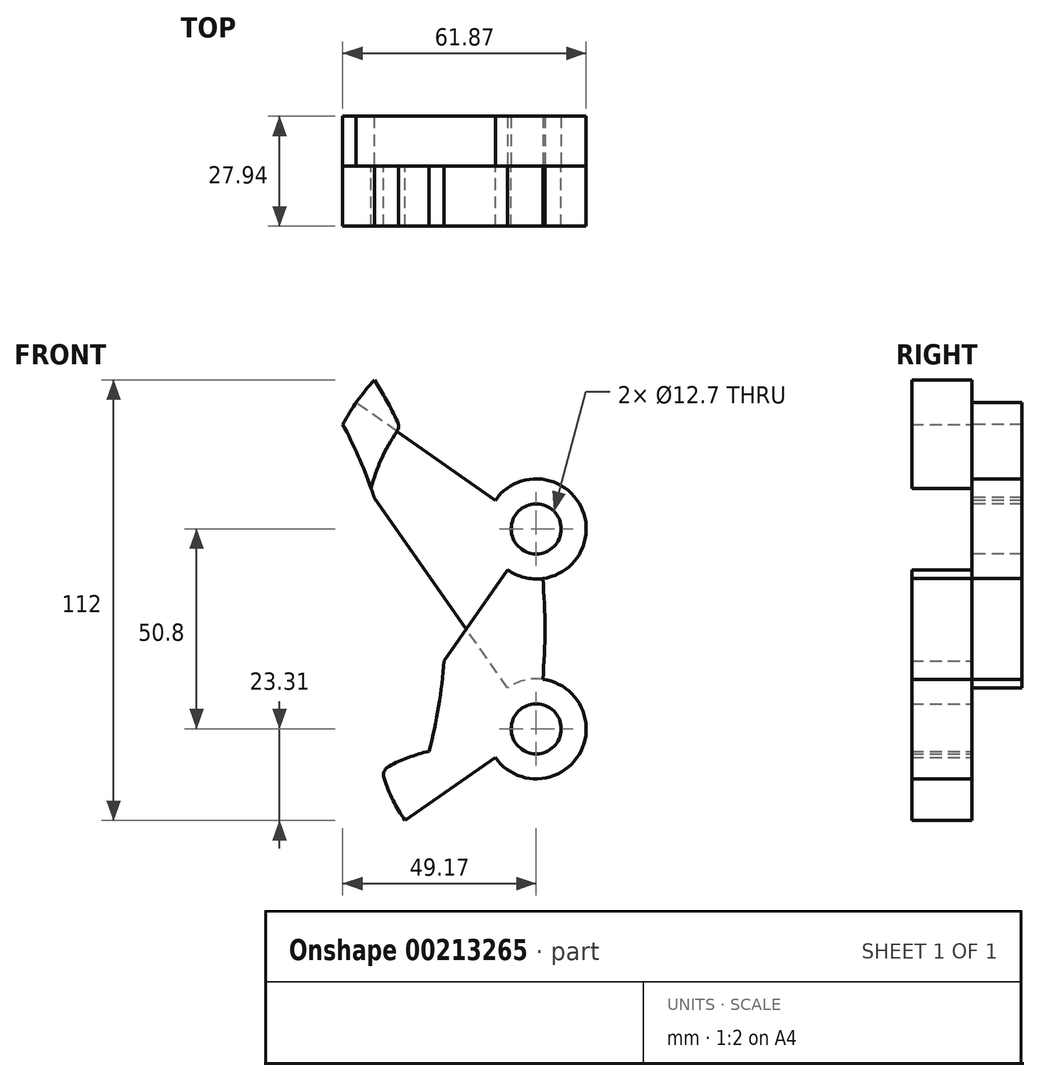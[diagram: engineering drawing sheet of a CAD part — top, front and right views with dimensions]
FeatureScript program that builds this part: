
annotation { "Feature Type Name" : "Feature", "Feature Type Description" : "" }
export const myFeature = defineFeature(function(context is Context, id is Id, definition is map)
    precondition{}
    {
        {
            var Q0;
            Q0=qCreatedBy(makeId("Front.planeOp"),FACE);
            var sketch = newSketch(context, id + "F0", { "sketchPlane" : qUnion([Q0])});
            skCircle(sketch, "E0", {"center": v(0, 0) * mm, "radius": 6.35 * mm});
            skCircle(sketch, "E1", {"center": v(0, 0) * mm, "radius": 12.7 * mm});
            skCircle(sketch, "E2", {"center": v(0, 50.8) * mm, "radius": 6.35 * mm});
            skCircle(sketch, "E3", {"center": v(0, 50.8) * mm, "radius": 12.7 * mm});
            skLineSegment(sketch, "E4", {"start": v(0, 0) * mm, "end": v(0, 50.8) * mm, "construction": true});
            skArc(sketch, "E5", {"start": v(-17.37, -47.74) * mm, "mid": v(0, 0) * mm, "end": v(0, 50.8) * mm});
            skLineSegment(sketch, "E6", {"start": v(-144.05, 25.4) * mm, "end": v(0, 0) * mm, "construction": true});
            skLineSegment(sketch, "E7", {"start": v(-144.05, 25.4) * mm, "end": v(0, 50.8) * mm, "construction": true});
            skLineSegment(sketch, "E8", {"start": v(0, 50.8) * mm, "end": v(-98.52, 119.79) * mm});
            skLineSegment(sketch, "E9", {"start": v(0, 50.8) * mm, "end": v(-66.69, -44.44) * mm});
            skLineSegment(sketch, "E10", {"start": v(0, 0) * mm, "end": v(-71.6, 102.25) * mm});
            skLineSegment(sketch, "E11", {"start": v(0, 0) * mm, "end": v(-89.4, -62.6) * mm});
            skArc(sketch, "E12", {"start": v(-41.27, -38.22) * mm, "mid": v(-23.24, 29.23) * mm, "end": v(-45.5, 95.4) * mm});
            skArc(sketch, "E13", {"start": v(-59.79, -42.43) * mm, "mid": v(-36.4, 36.04) * mm, "end": v(-74.7, 108.42) * mm});
            skLineSegment(sketch, "E14", {"start": v(-144.05, 25.4) * mm, "end": v(36.46, -78.82) * mm, "construction": true});
            skArc(sketch, "E15", {"start": v(-42.88, -12.9) * mm, "mid": v(-35.43, -8.51) * mm, "end": v(-27.25, -5.7) * mm});
            skArc(sketch, "E16", {"start": v(-37.97, 4.2) * mm, "mid": v(-31.34, 6.37) * mm, "end": v(-24.48, 7.69) * mm});
            skArc(sketch, "E17", {"start": v(-35.89, 24.01) * mm, "mid": v(-30.38, 30.68) * mm, "end": v(-23.65, 36.12) * mm});
            skArc(sketch, "E18", {"start": v(-37.12, 41.77) * mm, "mid": v(-31.63, 46.07) * mm, "end": v(-25.64, 49.65) * mm});
            skArc(sketch, "E19", {"start": v(-41.94, 61.1) * mm, "mid": v(-39.04, 69.24) * mm, "end": v(-34.58, 76.66) * mm});
            skArc(sketch, "E20", {"start": v(-49.17, 77.35) * mm, "mid": v(-45.48, 83.27) * mm, "end": v(-41.07, 88.7) * mm});
            skArc(sketch, "E21", {"start": v(-40.3, -5.22) * mm, "mid": v(-37.9, -14.7) * mm, "end": v(-33.3, -23.31) * mm});
            skSolve(sketch);
        }
        {
            var Q0;
            {var subQ0=sQuery(id+"F0.wireOp",EDGE,"E21");var subQ1=sQuery(id+"F0.wireOp",EDGE,"E11");var subQ2=makeQuery(id+"F0.imprint","INTERSECT",VERTEX,{"derivedFrom":[subQ1,subQ0]});Q0=makeQuery(id+"F0.imprint","IMPRINT",FACE,{"disambiguationData":[TD([[makeQuery(id+"F0.imprint","IMPRINT",EDGE,{"disambiguationData":[TD([[subQ2,1.0]])],"derivedFrom":subQ1}),-1.0]])]});}
            var Q1;
            {var subQ1=sQuery(id+"F0.wireOp",EDGE,"E11");var subQ3=sQuery(id+"F0.wireOp",EDGE,"E1");var subQ4=makeQuery(id+"F0.imprint","INTERSECT",VERTEX,{"derivedFrom":[subQ3,subQ1]});Q1=makeQuery(id+"F0.imprint","IMPRINT",FACE,{"disambiguationData":[TD([[makeQuery(id+"F0.imprint","IMPRINT",EDGE,{"disambiguationData":[TD([[subQ4,1.0]])],"derivedFrom":subQ3}),-1.0]])]});}
            var Q2;
            {var subQ0=sQuery(id+"F0.wireOp",EDGE,"E10");var subQ1=sQuery(id+"F0.wireOp",EDGE,"E0");var subQ2=makeQuery(id+"F0.imprint","INTERSECT",VERTEX,{"derivedFrom":[subQ1,subQ0]});Q2=makeQuery(id+"F0.imprint","IMPRINT",FACE,{"disambiguationData":[TD([[makeQuery(id+"F0.imprint","IMPRINT",EDGE,{"disambiguationData":[TD([[subQ2,-1.0]])],"derivedFrom":subQ1}),-1.0]])]});}
            var Q3;
            {var subQ0=sQuery(id+"F0.wireOp",EDGE,"E11");var subQ1=sQuery(id+"F0.wireOp",EDGE,"E0");var subQ2=makeQuery(id+"F0.imprint","INTERSECT",VERTEX,{"derivedFrom":[subQ1,subQ0]});Q3=makeQuery(id+"F0.imprint","IMPRINT",FACE,{"disambiguationData":[TD([[makeQuery(id+"F0.imprint","IMPRINT",EDGE,{"disambiguationData":[TD([[subQ2,-1.0]])],"derivedFrom":subQ1}),-1.0]])]});}
            var Q4;
            {var subQ0=sQuery(id+"F0.wireOp",EDGE,"E5");var subQ1=sQuery(id+"F0.wireOp",EDGE,"E0");var subQ2=makeQuery(id+"F0.imprint","INTERSECT",VERTEX,{"disambiguationData":[OD(0.0)],"derivedFrom":[subQ1,subQ0]});Q4=makeQuery(id+"F0.imprint","IMPRINT",FACE,{"disambiguationData":[TD([[makeQuery(id+"F0.imprint","IMPRINT",EDGE,{"disambiguationData":[TD([[subQ2,1.0]])],"derivedFrom":subQ1}),-1.0]])]});}
            var Q5;
            {var subQ0=sQuery(id+"F0.wireOp",EDGE,"E10");var subQ1=sQuery(id+"F0.wireOp",EDGE,"E0");var subQ2=makeQuery(id+"F0.imprint","INTERSECT",VERTEX,{"derivedFrom":[subQ1,subQ0]});Q5=makeQuery(id+"F0.imprint","IMPRINT",FACE,{"disambiguationData":[TD([[makeQuery(id+"F0.imprint","IMPRINT",EDGE,{"disambiguationData":[TD([[subQ2,1.0]])],"derivedFrom":subQ1}),-1.0]])]});}
            var Q6;
            {var subQ0=sQuery(id+"F0.wireOp",EDGE,"E20");var subQ1=sQuery(id+"F0.wireOp",EDGE,"E8");var subQ2=makeQuery(id+"F0.imprint","INTERSECT",VERTEX,{"derivedFrom":[subQ1,subQ0]});Q6=makeQuery(id+"F0.imprint","IMPRINT",FACE,{"disambiguationData":[TD([[makeQuery(id+"F0.imprint","IMPRINT",EDGE,{"disambiguationData":[TD([[subQ2,1.0]])],"derivedFrom":subQ1}),1.0]])]});}
            var Q7;
            {var subQ0=sQuery(id+"F0.wireOp",EDGE,"E20");var subQ1=sQuery(id+"F0.wireOp",EDGE,"E8");var subQ2=makeQuery(id+"F0.imprint","INTERSECT",VERTEX,{"derivedFrom":[subQ1,subQ0]});Q7=makeQuery(id+"F0.imprint","IMPRINT",FACE,{"disambiguationData":[TD([[makeQuery(id+"F0.imprint","IMPRINT",EDGE,{"disambiguationData":[TD([[subQ2,1.0]])],"derivedFrom":subQ1}),-1.0]])]});}
            var Q8;
            {var subQ0=sQuery(id+"F0.wireOp",EDGE,"E5");var subQ1=sQuery(id+"F0.wireOp",EDGE,"E1");var subQ2=makeQuery(id+"F0.imprint","INTERSECT",VERTEX,{"disambiguationData":[OD(1.0)],"derivedFrom":[subQ1,subQ0]});Q8=makeQuery(id+"F0.imprint","IMPRINT",FACE,{"disambiguationData":[TD([[makeQuery(id+"F0.imprint","IMPRINT",EDGE,{"disambiguationData":[TD([[subQ2,-1.0]])],"derivedFrom":subQ1}),-1.0]])]});}
            var Q9;
            {var subQ0=sQuery(id+"F0.wireOp",EDGE,"E15");var subQ1=sQuery(id+"F0.wireOp",EDGE,"E12");var subQ2=makeQuery(id+"F0.imprint","INTERSECT",VERTEX,{"derivedFrom":[subQ1,subQ0]});Q9=makeQuery(id+"F0.imprint","IMPRINT",FACE,{"disambiguationData":[TD([[makeQuery(id+"F0.imprint","IMPRINT",EDGE,{"disambiguationData":[TD([[subQ2,1.0]])],"derivedFrom":subQ1}),1.0]])]});}
            extrude(context, id + "F1", {"entities" : qUnion([Q0, Q1, Q2, Q3, Q4, Q5, Q6, Q7, Q8, Q9]), "depth" : 15.24 * mm});
        }
        {
            var Q0;
            {var subQ0=sQuery(id+"F0.wireOp",EDGE,"E20");var subQ1=sQuery(id+"F0.wireOp",EDGE,"E8");var subQ2=makeQuery(id+"F0.imprint","INTERSECT",VERTEX,{"derivedFrom":[subQ1,subQ0]});Q0=makeQuery(id+"F0.imprint","IMPRINT",FACE,{"disambiguationData":[TD([[makeQuery(id+"F0.imprint","IMPRINT",EDGE,{"disambiguationData":[TD([[subQ2,1.0]])],"derivedFrom":subQ1}),1.0]])]});}
            var Q1;
            {var subQ6=sQuery(id+"F0.wireOp",EDGE,"E12");var subQ8=sQuery(id+"F0.wireOp",EDGE,"E8");var subQ9=makeQuery(id+"F0.imprint","INTERSECT",VERTEX,{"derivedFrom":[subQ8,subQ6]});Q1=makeQuery(id+"F0.imprint","IMPRINT",FACE,{"disambiguationData":[TD([[makeQuery(id+"F0.imprint","IMPRINT",EDGE,{"disambiguationData":[TD([[subQ9,-1.0]])],"derivedFrom":subQ8}),1.0]])]});}
            var Q2;
            {var subQ5=sQuery(id+"F0.wireOp",EDGE,"E3");var subQ7=sQuery(id+"F0.wireOp",EDGE,"E8");var subQ8=makeQuery(id+"F0.imprint","INTERSECT",VERTEX,{"derivedFrom":[subQ5,subQ7]});Q2=makeQuery(id+"F0.imprint","IMPRINT",FACE,{"disambiguationData":[TD([[makeQuery(id+"F0.imprint","IMPRINT",EDGE,{"disambiguationData":[TD([[subQ8,-1.0]])],"derivedFrom":subQ5}),-1.0]])]});}
            var Q3;
            {var subQ0=sQuery(id+"F0.wireOp",EDGE,"E5");var subQ1=sQuery(id+"F0.wireOp",EDGE,"E1");var subQ2=makeQuery(id+"F0.imprint","INTERSECT",VERTEX,{"disambiguationData":[OD(1.0)],"derivedFrom":[subQ1,subQ0]});Q3=makeQuery(id+"F0.imprint","IMPRINT",FACE,{"disambiguationData":[TD([[makeQuery(id+"F0.imprint","IMPRINT",EDGE,{"disambiguationData":[TD([[subQ2,-1.0]])],"derivedFrom":subQ1}),-1.0]])]});}
            var Q4;
            {var subQ0=sQuery(id+"F0.wireOp",EDGE,"E9");var subQ1=sQuery(id+"F0.wireOp",EDGE,"E2");var subQ2=makeQuery(id+"F0.imprint","INTERSECT",VERTEX,{"derivedFrom":[subQ1,subQ0]});Q4=makeQuery(id+"F0.imprint","IMPRINT",FACE,{"disambiguationData":[TD([[makeQuery(id+"F0.imprint","IMPRINT",EDGE,{"disambiguationData":[TD([[subQ2,1.0]])],"derivedFrom":subQ1}),-1.0]])]});}
            var Q5;
            {var subQ0=sQuery(id+"F0.wireOp",EDGE,"E8");var subQ1=sQuery(id+"F0.wireOp",EDGE,"E2");var subQ2=makeQuery(id+"F0.imprint","INTERSECT",VERTEX,{"derivedFrom":[subQ1,subQ0]});Q5=makeQuery(id+"F0.imprint","IMPRINT",FACE,{"disambiguationData":[TD([[makeQuery(id+"F0.imprint","IMPRINT",EDGE,{"disambiguationData":[TD([[subQ2,1.0]])],"derivedFrom":subQ1}),-1.0]])]});}
            var Q6;
            {var subQ0=sQuery(id+"F0.wireOp",EDGE,"E9");var subQ1=sQuery(id+"F0.wireOp",EDGE,"E2");var subQ2=makeQuery(id+"F0.imprint","INTERSECT",VERTEX,{"derivedFrom":[subQ1,subQ0]});Q6=makeQuery(id+"F0.imprint","IMPRINT",FACE,{"disambiguationData":[TD([[makeQuery(id+"F0.imprint","IMPRINT",EDGE,{"disambiguationData":[TD([[subQ2,-1.0]])],"derivedFrom":subQ1}),-1.0]])]});}
            var Q7;
            {var subQ0=sQuery(id+"F0.wireOp",EDGE,"E17");var subQ1=sQuery(id+"F0.wireOp",EDGE,"E10");var subQ2=makeQuery(id+"F0.imprint","INTERSECT",VERTEX,{"derivedFrom":[subQ1,subQ0]});Q7=makeQuery(id+"F0.imprint","IMPRINT",FACE,{"disambiguationData":[TD([[makeQuery(id+"F0.imprint","IMPRINT",EDGE,{"disambiguationData":[TD([[subQ2,-1.0]])],"derivedFrom":subQ1}),-1.0]])]});}
            var Q8;
            {var subQ0=sQuery(id+"F0.wireOp",EDGE,"E12");var subQ1=sQuery(id+"F0.wireOp",EDGE,"E10");var subQ2=makeQuery(id+"F0.imprint","INTERSECT",VERTEX,{"derivedFrom":[subQ1,subQ0]});Q8=makeQuery(id+"F0.imprint","IMPRINT",FACE,{"disambiguationData":[TD([[makeQuery(id+"F0.imprint","IMPRINT",EDGE,{"disambiguationData":[TD([[subQ2,-1.0]])],"derivedFrom":subQ1}),-1.0]])]});}
            extrude(context, id + "F2", {"entities" : qUnion([Q0, Q1, Q2, Q3, Q4, Q5, Q6, Q7, Q8]), "oppositeDirection" : true, "depth" : 12.7 * mm});
        }
        {
            var Q0;
            Q0=makeQuery(id+"F1.opExtrude","SWEPT_EDGE",EDGE,{"disambiguationData":[OSD([sQuery(id+"F0.wireOp",EDGE,"E15"),sQuery(id+"F0.wireOp",EDGE,"E21")])]});
            var Q1;
            Q1=makeQuery(id+"F1.opExtrude","SWEPT_EDGE",EDGE,{"disambiguationData":[OSD([sQuery(id+"F0.wireOp",EDGE,"E12"),sQuery(id+"F0.wireOp",EDGE,"E19")])]});
            fillet(context, id + "F3", {"entities" : qUnion([Q0, Q1]), "radius" : 2.54 * mm, "tangentPropagation" : true, "allowEdgeOverflow" : false});
        }
    });
